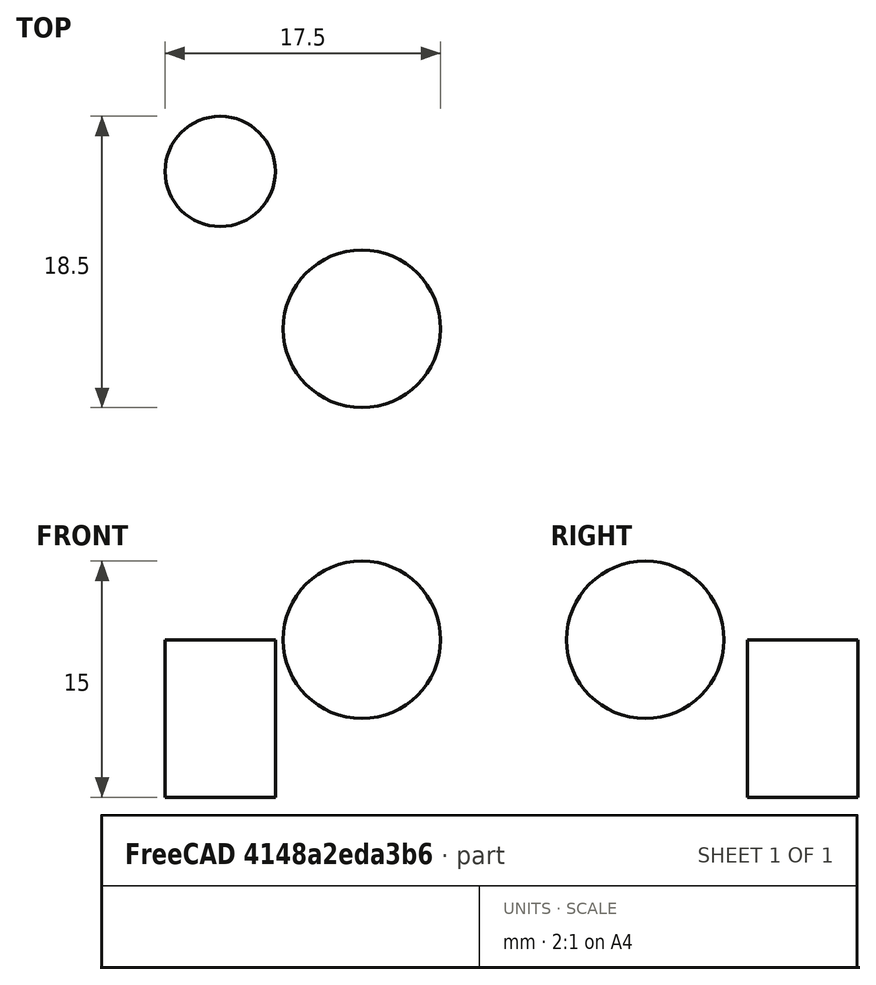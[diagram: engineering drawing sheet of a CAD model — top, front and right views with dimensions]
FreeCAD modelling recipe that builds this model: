
FCSTD DOCUMENT  (FreeCAD 0.17R10236 (Git))
Label: Sketch_on_surface
License: All rights reserved
LicenseURL: http://en.wikipedia.org/wiki/All_rights_reserved
objects: Sketcher::SketchObject×2, Part::Cylinder×1, Part::Sphere×1, Part::Feature×1
note: 5 computed .brp shape members not serialized (recipe doc carries the construction recipe); baked Part::Feature solids carry a one-line shape summary decoded from their .brp

FEATURE [Part::Cylinder] Cylinder
  Angle = 360
  AttacherType = Attacher::AttachEngine3D
  Height = 10
  Placement = pos=(0,10,0) rot=(0,0,1;0rad)
  Radius = 3.5
FEATURE [Sketcher::SketchObject] Sketch
  Placement = pos=(-2,-15,0) rot=(0,0,1;0rad)
  expr: Constraints[9] = 2 * pi
  sketch-geometry (12):
    g0: LineSegment StartX=0 StartY=0 StartZ=0 EndX=6.28319 EndY=0 EndZ=0
    g1: LineSegment StartX=6.28319 StartY=0 StartZ=0 EndX=6.28319 EndY=10 EndZ=0
    g2: LineSegment StartX=6.28319 StartY=10 StartZ=0 EndX=0 EndY=10 EndZ=0
    g3: LineSegment StartX=0 StartY=10 StartZ=0 EndX=0 EndY=0 EndZ=0
    g4: LineSegment StartX=0 StartY=8 StartZ=0 EndX=1.02467 EndY=8 EndZ=0
    g5: LineSegment StartX=2.08313 StartY=6.94155 StartZ=0 EndX=2.08313 EndY=3.94154 EndZ=0
    g6: LineSegment StartX=4.20005 StartY=3.94155 StartZ=0 EndX=4.20005 EndY=6.94155 EndZ=0
    g7: LineSegment StartX=5.25851 StartY=8.00001 StartZ=0 EndX=6.28319 EndY=8.00001 EndZ=0
    g8: ArcOfCircle CenterX=1.02467 CenterY=6.94154 CenterZ=0 NormalX=0 NormalY=0 NormalZ=1 Radius=1.05846 StartAngle=6.83352e-06 EndAngle=1.5708
    g9: ArcOfCircle CenterX=3.14159 CenterY=3.94155 CenterZ=0 NormalX=0 NormalY=0 NormalZ=1 Radius=1.05846 StartAngle=3.1416 EndAngle=6.28319
    g10: ArcOfCircle CenterX=5.25851 CenterY=6.94155 CenterZ=0 NormalX=0 NormalY=0 NormalZ=1 Radius=1.05846 StartAngle=1.5708 EndAngle=3.14159
    g11: Circle CenterX=3.11886 CenterY=1.5 CenterZ=0 NormalX=0 NormalY=0 NormalZ=1 Radius=1
  constraints (37):
    c: Coincident(g0,g1)
    c: Coincident(g1,g2)
    c: Coincident(g2,g3)
    c: Coincident(g3,g0)
    c: Horizontal(g0)
    c: Horizontal(g2)
    c: Vertical(g1)
    c: Vertical(g3)
    c: Coincident(g0,g-1)
    c: DistanceX(g2,g2) = 6.28319
    c: DistanceY(g3,g3) = 10
    c: PointOnObject(g4,g3)
    c: Horizontal(g4)
    c: Vertical(g5)
    c: Vertical(g6)
    c: Horizontal(g7)
    c: PointOnObject(g7,g1)
    c: Coincident(g8,g4)
    c: Coincident(g8,g5)
    c: Coincident(g10,g6)
    c: Coincident(g10,g7)
    c: Tangent(g9,g6) = -1.5708
    c: Tangent(g9,g5)
    c: Tangent(g4,g8)
    c: Tangent(g8,g5)
    c: Tangent(g7,g10)
    c: Tangent(g6,g10)
    c: Equal(g4,g7)
    c: Equal(g8,g10)
    c: Equal(g8,g9)
    c: Equal(g5,g6)
    c: Radius(g8) = 1.05846
    c: DistanceY(g9,g5) = 3
    c: DistanceY(g4,g2) = 2
    c: Coincident(g9,g5)
    c: Radius(g11) = 1
    c: DistanceY(g-1,g11) = 1.5
FEATURE [Part::Sphere] Sphere
  Angle1 = -90
  Angle2 = 90
  Angle3 = 360
  AttacherType = Attacher::AttachEngine3D
  Placement = pos=(9,0,10) rot=(0,0,1;0rad)
  Radius = 5
FEATURE [Part::Feature] Shape001
  shape: bbox 7.922 x 5.383 x 10.25 mm, 1 faces, 0 solids (baked)
FEATURE [Sketcher::SketchObject] Sketch001
  Placement = pos=(-5,-5,0) rot=(0,0,1;0rad)
  sketch-geometry (11):
    g0: LineSegment StartX=0 StartY=0 StartZ=0 EndX=1 EndY=0 EndZ=0
    g1: LineSegment StartX=1 StartY=0 StartZ=0 EndX=1 EndY=1 EndZ=0
    g2: LineSegment StartX=1 StartY=1 StartZ=0 EndX=0 EndY=1 EndZ=0
    g3: LineSegment StartX=0 StartY=1 StartZ=0 EndX=0 EndY=0 EndZ=0
    g4: Circle CenterX=0.14811 CenterY=0.847516 CenterZ=0 NormalX=0 NormalY=0 NormalZ=1 Radius=0.103975
    g5: Circle CenterX=0.516288 CenterY=0.847516 CenterZ=0 NormalX=0 NormalY=0 NormalZ=1 Radius=0.107159
    g6: Circle CenterX=0.348934 CenterY=0.492726 CenterZ=0 NormalX=0 NormalY=0 NormalZ=1 Radius=0.23194
    g7: Circle CenterX=0.837607 CenterY=0.727021 CenterZ=0 NormalX=0 NormalY=0 NormalZ=1 Radius=0.143105
    g8: Circle CenterX=0.757277 CenterY=0.308637 CenterZ=0 NormalX=0 NormalY=0 NormalZ=1 Radius=0.194159
    g9: Circle CenterX=0.425917 CenterY=0.131242 CenterZ=0 NormalX=0 NormalY=0 NormalZ=1 Radius=0.093239
    g10: Circle CenterX=0.134722 CenterY=0.161366 CenterZ=0 NormalX=0 NormalY=0 NormalZ=1 Radius=0.09637
  constraints (11):
    c: Coincident(g0,g1)
    c: Coincident(g1,g2)
    c: Coincident(g2,g3)
    c: Coincident(g3,g0)
    c: Horizontal(g0)
    c: Horizontal(g2)
    c: Vertical(g1)
    c: Vertical(g3)
    c: Coincident(g0,g-1)
    c: DistanceX(g2,g2) = 1
    c: DistanceY(g3,g3) = 1
